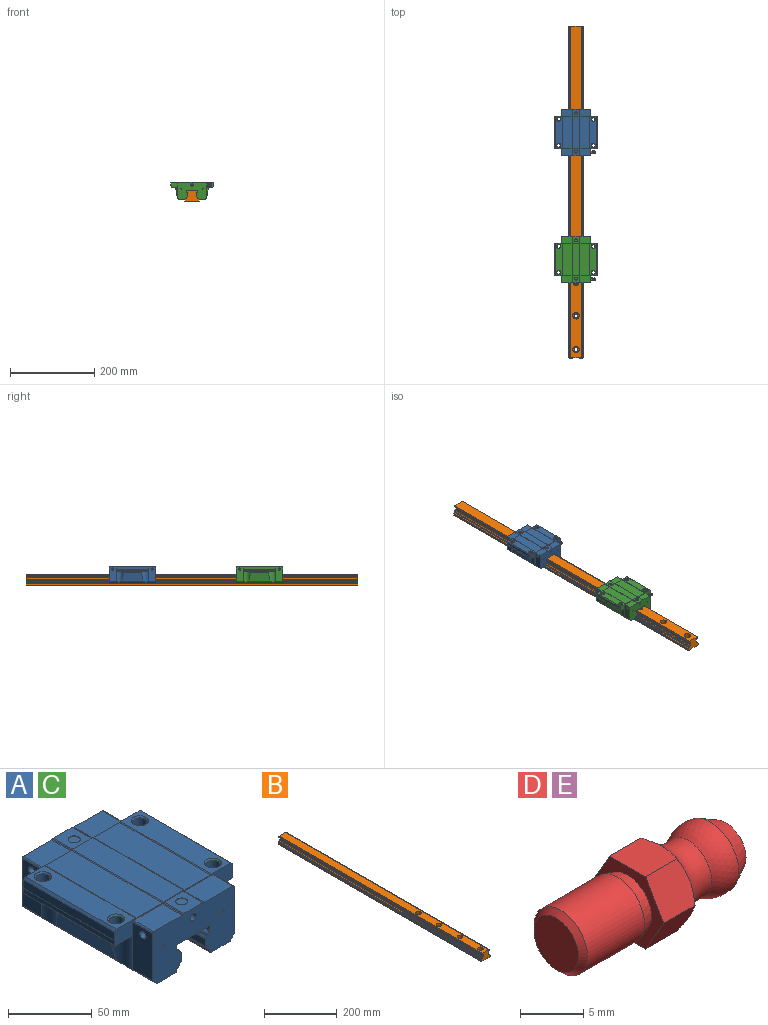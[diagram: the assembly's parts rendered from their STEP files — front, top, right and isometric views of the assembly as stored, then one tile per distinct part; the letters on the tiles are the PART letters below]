
ASSEMBLY  parts=5 mates=4
PART A: 156 faces, bbox 100x110.5x40.4 mm
  f0: cone r=5.25mm half-angle=45deg, axis (0,0,-1), area 42.2mm2, adj f4,f8
  f1: cone r=5.25mm half-angle=45deg, axis (0,0,-1), area 42.2mm2, adj f5,f11
  f2: cylinder r=4.25mm len=10.08mm, axis (0,0,1), area 269.2mm2, adj f7,f13
  f3: cylinder r=4.25mm len=10.08mm, axis (0,0,1), area 269.2mm2, adj f6,f14
  f4: cylinder r=4.25mm len=10.08mm, axis (0,0,1), area 269.2mm2, adj f0,f22
  f5: cylinder r=4.25mm len=10.08mm, axis (0,0,1), area 269.2mm2, adj f1,f23
  f6: cone r=5.25mm half-angle=45deg, axis (0,0,-1), area 42.2mm2, adj f3,f24
  f7: cone r=5.25mm half-angle=45deg, axis (0,0,-1), area 42.2mm2, adj f2,f25
  f8: cylinder r=5.25mm len=10.5mm, axis (0,0,1), area 0.3mm2, adj f0,f39
  f9: plane 77x0.3mm, normal (-0.71,0,-0.71), area 32.7mm2, adj f49,f50,f77,f109
  f10: plane 77x0.8mm, normal (-0.71,0,-0.71), area 70.8mm2, adj f39,f41,f50,f51,f77,f96,f98,f109
  f11: cylinder r=5.25mm len=10.5mm, axis (0,0,1), area 0.3mm2, adj f1,f51
  f12: plane 77x0.01mm, normal (-0.71,0,0.71), area 0.8mm2, adj f15,f55,f77,f109
  f13: cone r=5.16mm half-angle=45deg, axis (0,0,1), area 38mm2, adj f2,f55
  f14: cone r=5.16mm half-angle=45deg, axis (0,0,1), area 38mm2, adj f3,f55
  f15: cylinder r=1mm len=77mm, axis (0,-1,0), area 60.5mm2, adj f12,f56,f77,f109
  f16: cylinder r=1mm len=77mm, axis (0,-1,0), area 60.5mm2, adj f17,f56,f77,f109
  f17: plane 77x0.01mm, normal (0.71,0,0.71), area 0.8mm2, adj f16,f57,f77,f109
  f18: plane 77x0.01mm, normal (-0.71,0,0.71), area 0.8mm2, adj f19,f57,f77,f109
  f19: cylinder r=1mm len=77mm, axis (0,-1,0), area 60.5mm2, adj f18,f58,f77,f109
  f20: cylinder r=1mm len=77mm, axis (0,-1,0), area 60.5mm2, adj f21,f58,f77,f109
  f21: plane 77x0.01mm, normal (0.71,0,0.71), area 0.8mm2, adj f20,f59,f77,f109
  f22: cone r=5.16mm half-angle=45deg, axis (0,0,1), area 38mm2, adj f4,f59
  f23: cone r=5.16mm half-angle=45deg, axis (0,0,1), area 38mm2, adj f5,f59
  f24: cylinder r=5.25mm len=10.5mm, axis (0,0,1), area 0.3mm2, adj f6,f61
  f25: cylinder r=5.25mm len=10.5mm, axis (0,0,1), area 0.3mm2, adj f7,f64
  f26: plane 77x0.8mm, normal (0.71,0,-0.71), area 70.9mm2, adj f53,f61,f64,f65,f77,f109,f111,f113
  f27: cone r=2.6mm half-angle=59deg, axis (1,0,0), area 24.8mm2, adj f69
  f28: plane 16.75x0.01mm, normal (0.71,0,0.71), area 0.3mm2, adj f70,f73,f77,f151
  f29: plane 7.2x7.2mm, normal (0,0,1), area 40.7mm2, adj f74
  f30: plane 16.75x0.01mm, normal (-0.71,0,0.71), area 0.3mm2, adj f72,f75,f77,f151
  f31: cone r=2.6mm half-angle=59deg, axis (-1,0,0), area 24.8mm2, adj f78
  f32: plane 110.5x1.37mm, normal (-1,0,0), area 151.2mm2, adj f68,f83,f151,f153
  f33: plane 110.5x1.15mm, normal (-0.71,0,-0.71), area 180.4mm2, adj f82,f84,f151,f153
  f34: plane 110.5x1.15mm, normal (-0.71,0,0.71), area 180.4mm2, adj f85,f86,f151,f153
  f35: plane 110.5x1.15mm, normal (0.71,0,0.71), area 180.4mm2, adj f87,f88,f151,f153
  f36: plane 110.5x1.37mm, normal (1,0,0), area 151.2mm2, adj f38,f90,f151,f153
  f37: plane 110.5x1.15mm, normal (0.71,0,-0.71), area 180.4mm2, adj f89,f91,f151,f153
  f38: cylinder r=0.8mm len=110.5mm, axis (0,-1,0), area 84.9mm2, adj f36,f92,f151,f153
  f39: plane 19.5x15.9mm, normal (0,0,-1), area 183.2mm2, adj f8,f10,f40,f77,f96
  f40: plane 24.28x0.07mm, normal (-1,0,0), area 1.8mm2, adj f39,f77,f95,f96
  f41: plane 39.34x6.71mm, normal (0,0,-1), area 257.4mm2, adj f10,f42,f96,f98
  f42: cylinder r=3.5mm len=42.85mm, axis (0,-1,0), area 201.6mm2, adj f41,f43,f96,f98
  f43: plane 50.95x20.9mm, normal (-0.98,0,-0.17), area 982.9mm2, adj f42,f96,f97,f98
  f44: cone r=2.6mm half-angle=59deg, axis (-1,0,0), area 24.8mm2, adj f101
  f45: plane 16.75x0.01mm, normal (-0.71,0,0.71), area 0.3mm2, adj f102,f104,f109,f153
  f46: plane 7.2x7.2mm, normal (0,0,1), area 40.7mm2, adj f106
  f47: plane 16.75x0.01mm, normal (0.71,0,0.71), area 0.3mm2, adj f105,f107,f109,f153
  f48: plane 77x1.5mm, normal (-0.71,0,0.71), area 163.3mm2, adj f49,f59,f77,f109
  f49: plane 77x6.2mm, normal (-1,0,0), area 477.4mm2, adj f9,f48,f77,f109
  f50: plane 77x3.5mm, normal (-1,0,0), area 269.5mm2, adj f9,f10,f77,f109
  f51: plane 19.5x15.9mm, normal (0,0,-1), area 183.2mm2, adj f10,f11,f52,f98,f109
  f52: plane 24.28x0.07mm, normal (-1,0,0), area 1.8mm2, adj f51,f98,f99,f109
  f53: plane 77x10.2mm, normal (1,0,0), area 785.4mm2, adj f26,f54,f77,f109
  f54: plane 77x1.3mm, normal (0.71,0,0.71), area 141.6mm2, adj f53,f55,f77,f109
  f55: plane 77x16.4mm, normal (0,0,1), area 1095.5mm2, adj f12,f13,f14,f54,f77,f109
  f56: plane 77x22.17mm, normal (0,0,1), area 1707.2mm2, adj f15,f16,f77,f109
  f57: plane 77x17.4mm, normal (0,0,1), area 1339.8mm2, adj f17,f18,f77,f109
  f58: plane 77x22.17mm, normal (0,0,1), area 1707.2mm2, adj f19,f20,f77,f109
  f59: plane 77x16.2mm, normal (0,0,1), area 1080.1mm2, adj f21,f22,f23,f48,f77,f109
  f60: cone r=2.6mm half-angle=59deg, axis (1,0,0), area 24.8mm2, adj f110
  f61: plane 19.5x16.2mm, normal (0,0,-1), area 189mm2, adj f24,f26,f62,f109,f111
  f62: plane 24.28x0.07mm, normal (1,0,0), area 1.8mm2, adj f61,f109,f111,f117
  f63: plane 24.28x0.07mm, normal (1,0,0), area 1.8mm2, adj f64,f77,f113,f114
  f64: plane 19.5x16.2mm, normal (0,0,-1), area 189mm2, adj f25,f26,f63,f77,f113
  f65: plane 39.34x7.01mm, normal (0,0,-1), area 269mm2, adj f26,f66,f111,f113
  f66: cylinder r=3.5mm len=42.85mm, axis (0,-1,0), area 201.6mm2, adj f65,f67,f111,f113
  f67: plane 50.95x20.9mm, normal (0.98,0,-0.17), area 982.9mm2, adj f66,f111,f112,f113
  f68: cylinder r=0.8mm len=110.5mm, axis (0,-1,0), area 84.9mm2, adj f32,f118,f151,f153
  f69: cylinder r=2.6mm len=8.1mm, axis (1,0,0), area 132.3mm2, adj f27,f123
  f70: cylinder r=1mm len=16.75mm, axis (0,1,0), area 13.2mm2, adj f28,f77,f124,f151
  f71: cylinder r=1mm len=16.75mm, axis (0,1,0), area 26.3mm2, adj f77,f123,f124,f151
  f72: cylinder r=1mm len=16.75mm, axis (0,1,0), area 13.2mm2, adj f30,f77,f125,f151
  f73: cylinder r=1mm len=16.75mm, axis (0,1,0), area 13.2mm2, adj f28,f77,f125,f151
  f74: cylinder r=3.6mm len=7.2mm, axis (0,0,1), area 9mm2, adj f29,f125
  f75: cylinder r=1mm len=16.75mm, axis (0,-1,0), area 13.2mm2, adj f30,f77,f126,f151
  f76: cylinder r=1mm len=16.75mm, axis (0,1,0), area 26.3mm2, adj f77,f126,f127,f151
  f77: plane 100x37.19mm, normal (0,-1,0), area 438.3mm2, adj f9,f10,f12,f15,f16,f17,f18,f19
  f78: cylinder r=2.6mm len=8.1mm, axis (1,0,0), area 132.3mm2, adj f31,f127
  f79: cone r=1.25mm half-angle=59deg, axis (0,-1,0), area 5.7mm2, adj f128
  f80: cone r=1.25mm half-angle=59deg, axis (0,-1,0), area 5.7mm2, adj f129
  f81: cone r=2.6mm half-angle=59deg, axis (0,-1,0), area 24.8mm2, adj f130
  f82: cylinder r=0.5mm len=110.5mm, axis (0,-1,0), area 30.8mm2, adj f33,f132,f151,f153
  f83: cylinder r=0.5mm len=110.5mm, axis (0,-1,0), area 74.2mm2, adj f32,f132,f151,f153
  f84: cylinder r=0.8mm len=110.5mm, axis (0,-1,0), area 69.4mm2, adj f33,f133,f151,f153
  f85: cylinder r=0.8mm len=110.5mm, axis (0,-1,0), area 69.4mm2, adj f34,f133,f151,f153
  f86: cylinder r=0.5mm len=110.5mm, axis (0,-1,0), area 30.8mm2, adj f34,f134,f151,f153
  f87: cylinder r=0.5mm len=110.5mm, axis (0,-1,0), area 30.8mm2, adj f35,f135,f151,f153
  f88: cylinder r=0.8mm len=110.5mm, axis (0,-1,0), area 69.4mm2, adj f35,f136,f151,f153
  f89: cylinder r=0.8mm len=110.5mm, axis (0,-1,0), area 69.4mm2, adj f37,f136,f151,f153
  f90: cylinder r=0.5mm len=110.5mm, axis (0,-1,0), area 74.2mm2, adj f36,f137,f151,f153
  f91: cylinder r=0.5mm len=110.5mm, axis (0,-1,0), area 30.8mm2, adj f37,f137,f151,f153
  f92: plane 110.5x0.23mm, normal (0.57,0,-0.82), area 31mm2, adj f38,f138,f151,f153
  f93: cylinder r=1mm len=110.5mm, axis (0,1,0), area 86.8mm2, adj f138,f139,f151,f153
  f94: cylinder r=1mm len=16.75mm, axis (0,-1,0), area 13.2mm2, adj f77,f127,f139,f151
  f95: cylinder r=1mm len=0.48mm, axis (0,1,0), area 0.1mm2, adj f40,f77,f96,f139
  f96: cylinder r=13mm len=26.1mm, axis (0,0,-1), area 431.8mm2, adj f10,f39,f40,f41,f42,f43,f95,f97
  f97: cylinder r=1mm len=51.96mm, axis (0,1,0), area 31.4mm2, adj f43,f96,f98,f139
  f98: cylinder r=13mm len=26.1mm, axis (0,0,-1), area 431.8mm2, adj f10,f41,f42,f43,f51,f52,f97,f99
  f99: cylinder r=1mm len=0.48mm, axis (0,1,0), area 0.1mm2, adj f52,f98,f109,f139
  f100: cylinder r=1mm len=16.75mm, axis (0,-1,0), area 13.2mm2, adj f109,f139,f140,f153
  f101: cylinder r=2.6mm len=8.1mm, axis (-1,0,0), area 132.3mm2, adj f44,f140
  f102: cylinder r=1mm len=16.75mm, axis (0,-1,0), area 13.2mm2, adj f45,f109,f141,f153
  f103: cylinder r=1mm len=16.75mm, axis (0,1,0), area 26.3mm2, adj f109,f140,f141,f153
  f104: cylinder r=1mm len=16.75mm, axis (0,1,0), area 13.2mm2, adj f45,f109,f142,f153
  f105: cylinder r=1mm len=16.75mm, axis (0,1,0), area 13.2mm2, adj f47,f109,f142,f153
  f106: cylinder r=3.6mm len=7.2mm, axis (0,0,1), area 9mm2, adj f46,f142
  f107: cylinder r=1mm len=16.75mm, axis (0,1,0), area 13.2mm2, adj f47,f109,f143,f153
  f108: cylinder r=1mm len=16.75mm, axis (0,1,0), area 26.3mm2, adj f109,f143,f144,f153
  f109: plane 100x37.19mm, normal (0,1,0), area 438.3mm2, adj f9,f10,f12,f15,f16,f17,f18,f19
  f110: cylinder r=2.6mm len=8.1mm, axis (-1,0,0), area 132.3mm2, adj f60,f144
  f111: cylinder r=13mm len=26.1mm, axis (0,0,-1), area 431.9mm2, adj f26,f61,f62,f65,f66,f67,f112,f117
  f112: cylinder r=1mm len=51.96mm, axis (0,1,0), area 31.4mm2, adj f67,f111,f113,f145
  f113: cylinder r=13mm len=26.1mm, axis (0,0,-1), area 431.9mm2, adj f26,f63,f64,f65,f66,f67,f112,f114
  f114: cylinder r=1mm len=0.48mm, axis (0,1,0), area 0.1mm2, adj f63,f77,f113,f145
  f115: cylinder r=1mm len=16.75mm, axis (0,1,0), area 13.2mm2, adj f77,f123,f145,f151
  f116: cylinder r=1mm len=16.75mm, axis (0,1,0), area 13.2mm2, adj f109,f144,f145,f153
  f117: cylinder r=1mm len=0.48mm, axis (0,1,0), area 0.1mm2, adj f62,f109,f111,f145
  f118: plane 110.5x0.23mm, normal (-0.57,0,-0.82), area 31mm2, adj f68,f146,f151,f153
  f119: cylinder r=1mm len=110.5mm, axis (0,1,0), area 86.8mm2, adj f145,f146,f151,f153
  f120: cone r=1.25mm half-angle=59deg, axis (0,1,0), area 5.7mm2, adj f147
  f121: cone r=1.25mm half-angle=59deg, axis (0,1,0), area 5.7mm2, adj f148
  f122: cone r=2.6mm half-angle=59deg, axis (0,1,0), area 24.8mm2, adj f149
  f123: plane 34.49x16.75mm, normal (1,0,0), area 556.4mm2, adj f69,f71,f77,f115,f151
  f124: plane 24.09x16.75mm, normal (0,0,1), area 403.4mm2, adj f70,f71,f77,f151
  f125: plane 16.75x15.97mm, normal (0,0,1), area 226.8mm2, adj f72,f73,f74,f77,f151
  f126: plane 24.09x16.75mm, normal (0,0,1), area 403.4mm2, adj f75,f76,f77,f151
  f127: plane 34.49x16.75mm, normal (-1,0,0), area 556.4mm2, adj f76,f77,f78,f94,f151
  f128: cylinder r=1.25mm len=8.5mm, axis (0,-1,0), area 66.8mm2, adj f79,f151
  f129: cylinder r=1.25mm len=8.5mm, axis (0,1,0), area 66.8mm2, adj f80,f151
  f130: cylinder r=2.6mm len=8.1mm, axis (0,-1,0), area 132.3mm2, adj f81,f151
  f131: cylinder r=0.5mm len=110.5mm, axis (0,-1,0), area 74.2mm2, adj f134,f151,f152,f153
  f132: cylinder r=2.86mm len=110.5mm, axis (0,-1,0), area 352.4mm2, adj f82,f83,f151,f153
  f133: plane 110.5x5.26mm, normal (-1,0,0), area 581mm2, adj f84,f85,f151,f153
  f134: cylinder r=2.86mm len=110.5mm, axis (0,-1,0), area 352.4mm2, adj f86,f131,f151,f153
  f135: cylinder r=2.86mm len=110.5mm, axis (0,-1,0), area 352.4mm2, adj f87,f150,f151,f153
  f136: plane 110.5x5.26mm, normal (1,0,0), area 581mm2, adj f88,f89,f151,f153
  f137: cylinder r=2.86mm len=110.5mm, axis (0,-1,0), area 352.4mm2, adj f90,f91,f151,f153
  f138: plane 110.5x15.96mm, normal (0,0,-1), area 1764.1mm2, adj f92,f93,f151,f153
  f139: plane 110.5x3.48mm, normal (-0.71,0,-0.71), area 483.5mm2, adj f77,f93,f94,f95,f96,f97,f98,f99
  f140: plane 34.49x16.75mm, normal (-1,0,0), area 556.4mm2, adj f100,f101,f103,f109,f153
  f141: plane 24.09x16.75mm, normal (0,0,1), area 403.4mm2, adj f102,f103,f109,f153
  f142: plane 16.75x15.97mm, normal (0,0,1), area 226.8mm2, adj f104,f105,f106,f109,f153
  f143: plane 24.09x16.75mm, normal (0,0,1), area 403.4mm2, adj f107,f108,f109,f153
  f144: plane 34.49x16.75mm, normal (1,0,0), area 556.4mm2, adj f108,f109,f110,f116,f153
  f145: plane 110.5x3.48mm, normal (0.71,0,-0.71), area 483.5mm2, adj f77,f109,f111,f112,f113,f114,f115,f116
  f146: plane 110.5x15.96mm, normal (0,0,-1), area 1764.1mm2, adj f118,f119,f151,f153
  f147: cylinder r=1.25mm len=8.5mm, axis (0,-1,0), area 66.8mm2, adj f120,f153
  f148: cylinder r=1.25mm len=8.5mm, axis (0,1,0), area 66.8mm2, adj f121,f153
  f149: cylinder r=2.6mm len=8.1mm, axis (0,-1,0), area 132.3mm2, adj f122,f153
  f150: cylinder r=0.5mm len=110.5mm, axis (0,-1,0), area 74.2mm2, adj f135,f151,f153,f154
  f151: plane 69x40mm, normal (0,-1,0), area 2211mm2, adj f28,f30,f32,f33,f34,f35,f36,f37
  f152: plane 110.5x3.28mm, normal (-1,0,0), area 362.9mm2, adj f131,f151,f153,f155
  f153: plane 69x40mm, normal (0,1,0), area 2211mm2, adj f32,f33,f34,f35,f36,f37,f38,f45
  f154: plane 110.5x3.28mm, normal (1,0,0), area 362.9mm2, adj f150,f151,f153,f155
  f155: plane 110.5x28.1mm, normal (0,0,-1), area 3105mm2, adj f151,f152,f153,f154
PART B: 62 faces, bbox 34x788x26.5 mm
  f0: plane 788x1.5mm, normal (0.71,0,-0.71), area 1671.6mm2, adj f1,f47,f48,f61
  f1: plane 788x7.49mm, normal (0,0,-1), area 5901.8mm2, adj f0,f2,f48,f61
  f2: plane 788x1.35mm, normal (-0.87,0,-0.5), area 1228.4mm2, adj f1,f3,f48,f61
  f3: cylinder r=0.8mm len=788mm, axis (0,-1,0), area 660.2mm2, adj f2,f4,f48,f61
  f4: plane 788x13.08mm, normal (0,0,-1), area 10049.6mm2, adj f3,f5,f48,f49,f52,f55,f58,f61
  f5: cylinder r=0.8mm len=788mm, axis (0,-1,0), area 660.2mm2, adj f4,f6,f48,f61
  f6: plane 788x1.35mm, normal (0.87,0,-0.5), area 1228.4mm2, adj f5,f7,f48,f61
  f7: plane 788x7.49mm, normal (0,0,-1), area 5901.8mm2, adj f6,f8,f48,f61
  f8: plane 788x1.5mm, normal (-0.71,0,-0.71), area 1671.6mm2, adj f7,f9,f48,f61
  f9: plane 788x4.02mm, normal (-1,0,0), area 3166.1mm2, adj f8,f10,f48,f61
  f10: cylinder r=0.8mm len=788mm, axis (0,-1,0), area 605.1mm2, adj f9,f11,f48,f61
  f11: plane 788x2.27mm, normal (-0.57,0,0.82), area 2181.5mm2, adj f10,f12,f48,f61
  f12: cylinder r=0.8mm len=788mm, axis (0,-1,0), area 605.1mm2, adj f11,f13,f48,f61
  f13: plane 788x1.37mm, normal (-1,0,0), area 1078mm2, adj f12,f14,f48,f61
  f14: cylinder r=0.5mm len=788mm, axis (0,-1,0), area 529.2mm2, adj f13,f15,f48,f61
  f15: cylinder r=2.86mm len=788mm, axis (0,-1,0), area 2513mm2, adj f14,f16,f48,f61
  f16: cylinder r=0.5mm len=788mm, axis (0,-1,0), area 219.5mm2, adj f15,f17,f48,f61
  f17: plane 788x1.15mm, normal (-0.71,0,0.71), area 1286.3mm2, adj f16,f18,f48,f61
  f18: cylinder r=0.8mm len=788mm, axis (0,-1,0), area 495.1mm2, adj f17,f19,f48,f61
  f19: plane 788x5.26mm, normal (-1,0,0), area 4143.1mm2, adj f18,f20,f48,f61
  f20: cylinder r=0.8mm len=788mm, axis (0,-1,0), area 495.1mm2, adj f19,f21,f48,f61
  f21: plane 788x1.15mm, normal (-0.71,0,-0.71), area 1286.3mm2, adj f20,f22,f48,f61
  f22: cylinder r=0.5mm len=788mm, axis (0,-1,0), area 219.5mm2, adj f21,f23,f48,f61
  f23: cylinder r=2.86mm len=788mm, axis (0,-1,0), area 2513mm2, adj f22,f24,f48,f61
  f24: cylinder r=0.5mm len=788mm, axis (0,-1,0), area 529.2mm2, adj f23,f25,f48,f61
  f25: plane 788x1.37mm, normal (-1,0,0), area 1080mm2, adj f24,f26,f48,f61
  f26: cylinder r=0.8mm len=788mm, axis (0,-1,0), area 825.2mm2, adj f25,f27,f48,f61
  f27: plane 788x0.53mm, normal (-0.26,0,0.97), area 429.7mm2, adj f26,f28,f48,f61
  f28: plane 788x25.86mm, normal (0,0,1), area 19671.5mm2, adj f27,f29,f48,f51,f54,f57,f60,f61
  f29: plane 788x0.53mm, normal (0.26,0,0.97), area 429.7mm2, adj f28,f30,f48,f61
  f30: cylinder r=0.8mm len=788mm, axis (0,-1,0), area 825.2mm2, adj f29,f31,f48,f61
  f31: plane 788x1.37mm, normal (1,0,0), area 1080mm2, adj f30,f32,f48,f61
  f32: cylinder r=0.5mm len=788mm, axis (0,-1,0), area 529.2mm2, adj f31,f33,f48,f61
  f33: cylinder r=2.86mm len=788mm, axis (0,-1,0), area 2513mm2, adj f32,f34,f48,f61
  f34: cylinder r=0.5mm len=788mm, axis (0,-1,0), area 219.5mm2, adj f33,f35,f48,f61
  f35: plane 788x1.15mm, normal (0.71,0,-0.71), area 1286.3mm2, adj f34,f36,f48,f61
  f36: cylinder r=0.8mm len=788mm, axis (0,-1,0), area 495.1mm2, adj f35,f37,f48,f61
  f37: plane 788x5.26mm, normal (1,0,0), area 4143.1mm2, adj f36,f38,f48,f61
  f38: cylinder r=0.8mm len=788mm, axis (0,-1,0), area 495.1mm2, adj f37,f39,f48,f61
  f39: plane 788x1.15mm, normal (0.71,0,0.71), area 1286.3mm2, adj f38,f40,f48,f61
  f40: cylinder r=0.5mm len=788mm, axis (0,-1,0), area 219.5mm2, adj f39,f41,f48,f61
  f41: cylinder r=2.86mm len=788mm, axis (0,-1,0), area 2513mm2, adj f40,f42,f48,f61
  f42: cylinder r=0.5mm len=788mm, axis (0,-1,0), area 529.2mm2, adj f41,f43,f48,f61
  f43: plane 788x1.37mm, normal (1,0,0), area 1078mm2, adj f42,f44,f48,f61
  f44: cylinder r=0.8mm len=788mm, axis (0,-1,0), area 605.1mm2, adj f43,f45,f48,f61
  f45: plane 788x2.27mm, normal (0.57,0,0.82), area 2181.5mm2, adj f44,f46,f48,f61
  f46: cylinder r=0.8mm len=788mm, axis (0,-1,0), area 605.1mm2, adj f45,f47,f48,f61
  f47: plane 788x4.02mm, normal (1,0,0), area 3166.1mm2, adj f0,f46,f48,f61
  f48: plane 34x26.5mm, normal (0,-1,0), area 671.6mm2, adj f0,f1,f2,f3,f4,f5,f6,f7
  f49: cylinder r=4.5mm len=13.75mm, axis (0,0,1), area 388.8mm2, adj f4,f50
  f50: plane 15x15mm, normal (0,0,1), area 113.1mm2, adj f49,f51
  f51: cylinder r=7.5mm len=15mm, axis (0,0,1), area 518.3mm2, adj f28,f50
  f52: cylinder r=4.5mm len=13.75mm, axis (0,0,1), area 388.8mm2, adj f4,f53
  f53: plane 15x15mm, normal (0,0,1), area 113.1mm2, adj f52,f54
  f54: cylinder r=7.5mm len=15mm, axis (0,0,1), area 518.3mm2, adj f28,f53
  f55: cylinder r=4.5mm len=13.75mm, axis (0,0,1), area 388.8mm2, adj f4,f56
  f56: plane 15x15mm, normal (0,0,1), area 113.1mm2, adj f55,f57
  f57: cylinder r=7.5mm len=15mm, axis (0,0,1), area 518.3mm2, adj f28,f56
  f58: cylinder r=4.5mm len=13.75mm, axis (0,0,1), area 388.8mm2, adj f4,f59
  f59: plane 15x15mm, normal (0,0,1), area 113.1mm2, adj f58,f60
  f60: cylinder r=7.5mm len=15mm, axis (0,0,1), area 518.3mm2, adj f28,f59
  f61: plane 34x26.5mm, normal (0,1,0), area 671.6mm2, adj f0,f1,f2,f3,f4,f5,f6,f7
PART C: same geometry as A
PART D: 21 faces, bbox 19.2x11.9x11.9 mm
  f0: plane 8.08x7mm, normal (-1,0,0), area 20.2mm2, adj f2,f5,f6,f7,f8,f9,f10
  f1: plane 5x5mm, normal (-1,0,0), area 19.6mm2, adj f4
  f2: cone r=2.66mm half-angle=17.1deg, axis (-1,0,0), area 20.8mm2, adj f0,f3
  f3: cylinder r=3mm len=6.38mm, axis (-1,0,0), area 120.3mm2, adj f2,f4
  f4: cone r=3mm half-angle=45deg, axis (1,0,0), area 12.2mm2, adj f1,f3
  f5: plane 3.94x3.53mm, normal (0,0.87,-0.5), area 15.2mm2, adj f0,f6,f10,f18,f19,f20
  f6: plane 4.09x3.68mm, normal (0,0.87,0.5), area 15.2mm2, adj f0,f5,f7,f17,f18,f20
  f7: plane 4.07x3.94mm, normal (0,0,1), area 15.2mm2, adj f0,f6,f8,f16,f17,f20
  f8: plane 3.94x3.53mm, normal (0,-0.87,0.5), area 15.2mm2, adj f0,f7,f9,f15,f16,f20
  f9: plane 3.94x3.53mm, normal (0,-0.87,-0.5), area 15.2mm2, adj f0,f8,f10,f14,f15,f20
  f10: plane 4.07x3.94mm, normal (0,0,-1), area 15.2mm2, adj f0,f5,f9,f14,f19,f20
  f11: plane 4.5x4.5mm, normal (1,0,0), area 15.9mm2, adj f12
  f12: cone r=3.19mm half-angle=28.4deg, axis (-1,0,0), area 33.9mm2, adj f11,f13
  f13: sphere r=3.25mm, area 50.7mm2, adj f12,f20
  f14: torus R=3.03mm, axis (-1,0,0), area 0.1mm2, adj f9,f10,f20
  f15: torus R=3.03mm, axis (-1,0,0), area 0.1mm2, adj f8,f9,f20
  f16: torus R=3.03mm, axis (-1,0,0), area 0.1mm2, adj f7,f8,f20
  f17: torus R=3.03mm, axis (-1,0,0), area 0.1mm2, adj f6,f7,f20
  f18: torus R=3.03mm, axis (-1,0,0), area 0.1mm2, adj f5,f6,f20
  f19: torus R=3.03mm, axis (-1,0,0), area 0.1mm2, adj f5,f10,f20
  f20: torus R=5.57mm, axis (-1,0,0), area 60mm2, adj f5,f6,f7,f8,f9,f10,f13,f14
PART E: same geometry as D
PLACE A t=(0,535.43,-1)mm
PLACE B at identity fixed
PLACE C t=(0,233.94,-1)mm
PLACE D t=(0,535.43,-1)mm
PLACE E t=(1.12,233.94,-1)mm
MATE fastened C.f31 <-> E.f2  axis (1,0,0) through (34.5,186.79,23)mm
MATE slider A.f151 <-> B.f48  axis (0,-1,0) through (0,480.18,9.5)mm
MATE fastened A.f31 <-> D.f2  axis (1,0,0) through (34.5,488.28,23)mm
MATE slider C.f151 <-> B.f48  axis (0,-1,0) through (0,178.69,9.5)mm
